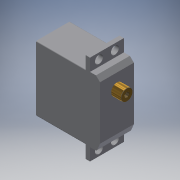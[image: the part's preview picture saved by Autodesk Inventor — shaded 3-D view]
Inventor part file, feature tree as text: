
AUTODESK INVENTOR PART (.ipt)
format: ipt  version: 2017 (Build 210142000, 142)  size: 173,056 bytes
history: native  units: mm
features: sketch x6, extrude x4, chamfer x3, hole x3, projected_geometry x2, fillet x1
ambient origin geometry x8: Origin, YZ Plane, XZ Plane, XY Plane, X Axis, Y Axis, Z Axis, Center Point
bodies: Solid1 (feature_tree)
feature tree (19):
  extrude  "Extrusion1"  Depth=32.7mm
  chamfer  "Chamfer1"  Distance=17.0mm
  chamfer  "Chamfer2"  Distance=2.0mm Angle=45.0deg
  extrude  "Extrusion2"  Depth=2.0mm
  extrude  "Extrusion3"  Depth=5.0mm TaperAngle=0.0deg
  hole  "Hole1"  [1 undecoded]
  extrude  "Extrusion4"  Depth=6.2mm
  hole  "Hole2"  [1 undecoded]
  chamfer  "Chamfer3"  Distance=3.0mm
  fillet  "Fillet1"  Radius=2.0mm
  hole  "Hole3"  [1 undecoded]
  sketch  "Sketch1"  dims[d0=32.0mm d1=32.7mm d2=17.0mm d3=0.0mm d4=2.0mm d5=2.0mm d6=45.0deg]
  sketch  "Sketch3"  dims[d7=2.0mm d8=2.0mm d9=45.0deg d10=9.2mm]
  sketch  "Sketch4"  dims[d11=5.8mm d12=5.0mm d13=0.0mm]
  sketch  "Sketch5"  dims[d14=5.0mm d15=2.2mm]
  projected_geometry  "Projected Loop2"
  sketch  "Sketch6"  dims[d16=6.2mm d17=0.0mm d18=3.0mm]
  projected_geometry  "Projected Loop3"
  sketch  "Sketch7"  dims[d19=8.0mm d20=4.0mm d21=6.0mm d22=4.0mm d23=2.0mm d24=90.0deg d25=8.0mm d26=20.594885mm d27=6.2mm d28=0.0mm d29=3.0mm d30=4.0mm d31=6.0mm d32=4.0mm d33=2.0mm d34=90.0deg d35=8.0mm d36=20.594885mm d37=0.1mm d38=2.0mm d39=45.0deg d40=0.5mm d41=10.0mm d42=10.0mm d43=2.459mm d44=5.0mm d45=4.0mm d46=2.0mm d47=90.0deg d48=6.0mm d49=20.594885mm]
note: 3 required parameter values undecoded (feature->parameter linkage not recoverable at this tier; creation-order binding heuristic only, values carry confidence <= 0.55)
